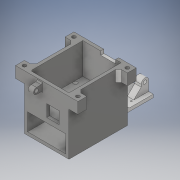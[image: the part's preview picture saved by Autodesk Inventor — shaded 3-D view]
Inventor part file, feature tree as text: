
AUTODESK INVENTOR PART (.ipt)
format: ipt  version: 2018 (Build 220112000, 112)  size: 1,372,160 bytes
history: native  units: in
note: dims shown in document units (in); Inventor stores cm internally (conversion verified against a paired STEP export)
features: sketch x43, extrude x40, move_body x18, direct_edit x15, chamfer x8, fillet x6, thicken_offset x3, delete_face x2, projected_geometry x2
ambient origin geometry x8: Origin, YZ Plane, XZ Plane, XY Plane, X Axis, Y Axis, Z Axis, Center Point
bodies: Solid1 (feature_tree)
feature tree (137):
  extrude  "Extrusion1"  Depth=0.125in
  extrude  "Extrusion2"  Depth=2.2in TaperAngle=0.0deg
  extrude  "Extrusion3"  Depth=0.125in
  extrude  "Extrusion4"  Depth=0.0625in
  sketch  "Sketch6"  dims[d11=0.5in d13=0.55in]
  extrude  "Extrusion6"  Depth=0.55in
  extrude  "Extrusion7"  Depth=0.725in
  extrude  "Extrusion8"  Depth=0.09in
  extrude  "Extrusion9"  Depth=0.125in
  extrude  "Extrusion10"  Depth=0.125in TaperAngle=0.0deg
  extrude  "Extrusion11"  Depth=0.7in
  extrude  "Extrusion12"  Depth=0.5in
  sketch  "Sketch16"  dims[d38=0.05in]
  extrude  "Extrusion13"  Depth=0.05in
  sketch  "Sketch18"  dims[d40=0.45in]
  fillet  "Fillet1"  Radius=0.05in
  chamfer  "Chamfer1"  Distance=0.36in
  chamfer  "Chamfer2"  Distance=0.25in
  extrude  "Extrusion14"  Depth=0.05in
  extrude  "Extrusion15"  Depth=0.35in
  extrude  "Extrusion16"  Depth=0.25in
  fillet  "Fillet2"  Radius=0.25in
  extrude  "Extrusion17"  Depth=0.1in
  chamfer  "Chamfer3"  Distance=0.05in Angle=45.0deg
  extrude  "Extrusion18"  Depth=0.125in
  extrude  "Extrusion19"  Depth=0.05in TaperAngle=0.0deg
  extrude  "Extrusion20"  Depth=0.05in
  extrude  "Extrusion21"  Depth=0.1in
  fillet  "Fillet3"  Radius=0.275in
  fillet  "Fillet4"  Radius=0.36in
  extrude  "Extrusion22"  Depth=0.225in
  extrude  "Extrusion23"  Depth=0.26in TaperAngle=0.0deg
  chamfer  "Chamfer4"  Distance=0.05in
  chamfer  "Chamfer5"  Distance=0.05in Angle=45.0deg
  extrude  "Extrusion24"  Depth=0.05in TaperAngle=0.0deg
  extrude  "Extrusion25"  Depth=0.125in TaperAngle=0.0deg
  extrude  "Extrusion28"  Depth=1.0in
  extrude  "Extrusion29"  Depth=1.0in
  extrude  "Extrusion30"  Depth=0.25in
  extrude  "Extrusion31"  Depth=0.25in
  thicken_offset  "Thicken1"
  thicken_offset  "Thicken2"
  thicken_offset  "Thicken3"
  direct_edit  "Direct Edit1"
  direct_edit  "Direct Edit2"
  direct_edit  "Direct Edit3"
  direct_edit  "Direct Edit4"
  extrude  "Extrusion32"  Depth=0.21in TaperAngle=0.0deg
  fillet  "Fillet5"  Radius=0.5in
  chamfer  "Chamfer7"  Distance=0.63in
  direct_edit  "Direct Edit5"
  direct_edit  "Direct Edit6"
  extrude  "Extrusion33"  Depth=0.25in
  extrude  "Extrusion34"  Depth=0.25in
  extrude  "Extrusion35"  Depth=0.25in
  direct_edit  "Direct Edit7"
  extrude  "Extrusion36"  Depth=0.25in
  direct_edit  "Direct Edit8"
  delete_face  "Delete Face1"
  direct_edit  "Direct Edit9"
  direct_edit  "Direct Edit10"
  extrude  "Extrusion37"  Depth=0.25in
  extrude  "Extrusion38"  Depth=0.25in
  fillet  "Fillet6"  Radius=0.437in
  extrude  "Extrusion39"  Depth=0.1in TaperAngle=0.0deg
  chamfer  "Chamfer9"  Distance=0.344in
  extrude  "Extrusion40"  Depth=0.25in
  extrude  "Extrusion41"  Depth=0.25in
  chamfer  "Chamfer10"  Distance=0.344in
  extrude  "Extrusion42"  Depth=0.1in TaperAngle=0.0deg
  extrude  "Extrusion43"  Depth=0.1in TaperAngle=45.0deg
  direct_edit  "Direct Edit11"
  direct_edit  "Direct Edit12"
  delete_face  "Delete Face2"
  direct_edit  "Direct Edit13"
  direct_edit  "Direct Edit14"
  direct_edit  "Direct Edit15"
  sketch  "Sketch1"  dims[d0=0.125in d1=1.24in]
  sketch  "Sketch2"  dims[d2=0.9in d3=2.2in d4=0.0in]
  sketch  "Sketch3"  dims[d5=0.125in d6=0.0in d7=2.0in]
  sketch  "Sketch4"  dims[d8=0.125in d9=0.0in d10=0.0625in]
  sketch  "Sketch8"  dims[d14=0.125in d15=0.0in d16=0.725in]
  sketch  "Sketch10"  dims[d17=2.06in d21=0.09in]
  sketch  "Sketch11"  dims[d22=0.4in d23=0.0in d24=0.125in]
  sketch  "Sketch12"  dims[d25=1.475in d26=0.0in d27=0.125in d28=0.0in]
  sketch  "Sketch13"  dims[d29=0.6in d30=0.7in]
  sketch  "Sketch14"  dims[d31=0.5in d32=0.0in d33=0.1603in]
  sketch  "Sketch15"  dims[d34=0.5in d35=0.0in d36=0.146in d37=0.05in]
  sketch  "Sketch17"  dims[d39=0.1in]
  sketch  "Sketch19"  dims[d41=1.0in d42=0.36in d43=0.0in]
  sketch  "Sketch20"  dims[d44=0.225in]
  sketch  "Sketch21"  dims[d45=0.146in d46=0.25in d47=0.0in]
  sketch  "Sketch22"  dims[d49=0.05in d50=0.0in d51=0.05in]
  sketch  "Sketch24"  dims[d52=0.05in d53=0.35in]
  sketch  "Sketch25"  dims[d54=0.02in d55=0.02in d56=0.25in]
  sketch  "Sketch26"  dims[d57=0.25in d58=0.1in]
  sketch  "Sketch27"  dims[d59=0.0in]
  sketch  "Sketch28"  dims[d60=0.35in]
  sketch  "Sketch29"  dims[d61=0.346in]
  sketch  "Sketch30"  dims[d62=0.425in]
  sketch  "Sketch31"  dims[d63=0.9in]
  sketch  "Sketch34"  dims[d64=0.123in]
  sketch  "Sketch35"  dims[d65=0.123in d66=0.05in d67=0.125in d68=45.0deg]
  sketch  "Sketch36"  dims[d69=0.05in d70=0.125in d71=45.0deg d72=0.01in]
  sketch  "Sketch37"  dims[d73=0.4in d74=0.05in d75=0.0in]
  projected_geometry  "Projected Loop1"
  sketch  "Sketch38"  dims[d76=0.146in d77=0.05in]
  sketch  "Sketch39"  dims[d78=0.05in d80=0.1in d81=0.275in d82=0.36in d83=0.0in]
  sketch  "Sketch40"  dims[d84=0.225in d85=0.01in]
  sketch  "Sketch41"  dims[d86=0.146in d87=0.26in d88=0.0in]
  sketch  "Sketch42"  dims[d89=0.123in]
  sketch  "Sketch43"  dims[d90=0.05in]
  sketch  "Sketch44"  dims[d91=0.05in d92=0.05in d93=0.0in d94=0.05in d95=0.125in d96=45.0deg]
  sketch  "Sketch45"  dims[d97=0.45in d98=0.05in d99=0.0in]
  sketch  "Sketch46"  dims[d100=0.125in d101=0.0in d102=0.125in d103=0.0in]
  sketch  "Sketch47"  dims[d104=1.0in d105=1.0in]
  projected_geometry  "Projected Loop2"
  sketch  "Sketch48"  dims[d106=1.0in d107=0.912in]
  sketch  "Sketch49"  dims[d108=0.912in d109=0.912in d110=0.912in d111=0.21in d112=0.0in d113=0.5in d114=0.63in d115=0.63in d116=0.63in d117=0.63in d118=0.437in d119=0.437in d120=0.437in d121=0.437in d122=0.1in d123=0.0in d124=0.344in d125=0.344in d126=0.344in d127=0.344in d128=0.1in d129=0.0in d130=0.1in d131=0.125in d132=45.0deg d133=0.05in d134=0.125in d135=45.0deg d139=0.312in d140=0.3603in d141=0.3603in d142=0.3603in d143=0.3603in d144=0.3603in d145=0.45in d146=0.0in d147=0.146in d148=0.146in d149=0.146in d150=0.146in d151=0.5in d152=0.0in d163=1.0in d164=0.0in d165=0.35in d166=1.5in d168=0.3in d169=1.0in d170=0.0in d171=0.05in d172=0.3in d173=0.0in d174=0.05in d175=0.0in d176=0.1in d177=0.1in d178=0.1in d179=0.1in d180=0.1in d181=0.1in d182=0.0in d183=0.0in d184=0.1in d185=0.0in d186=0.0in d187=-0.1in d188=0.0in d189=0.0in d190=-0.05in d191=0.5in d192=0.0in d193=0.0in d194=0.05in d195=0.937in d196=0.937in d197=0.937in d198=0.937in d199=0.375in d200=0.0in d201=0.5in d202=0.125in d203=0.125in d204=45.0deg d205=0.0in d206=0.0in d207=-0.175in d208=0.0in d209=0.0in d210=0.35in d211=0.0in d212=0.0in d213=0.105in d214=0.0in d215=0.0in d216=0.105in d217=0.16in d218=1.0in d219=0.0in d220=3.9056in d221=0.6in d222=0.0in d223=0.0in d224=3.9in d225=0.6in d226=1.0in d227=0.0in d228=0.0in d229=0.0in d230=0.2in d231=0.0in d232=0.0in d233=0.0in d234=0.0in d235=0.7in d236=0.0in d237=0.0in d238=-0.065in d239=0.0in d240=0.0in d241=-1.54in d242=0.125in d243=0.9in d244=1.5in d245=0.0in d249=0.26in d250=0.3in d251=0.19in d252=0.55in d253=0.0in d254=0.15in d255=0.146in d256=0.36in d257=0.0in d258=0.3in d259=0.125in d260=45.0deg d261=0.1in d262=0.0in d263=0.1in d264=0.0in d265=0.1in d266=0.125in d267=45.0deg d268=0.6in d269=0.15in d270=0.0in d271=0.1in d272=0.0in d273=0.06in d274=0.06in d275=0.25in d276=0.25in d277=0.1in d278=0.0in d279=45.0deg d280=0.75in d281=0.2in d282=0.0in d283=0.0in d284=0.0in d285=0.0in d286=0.02in d287=0.0in d288=0.0in d289=0.09in d290=0.25in d291=0.0in d292=0.0in d293=0.0in d294=0.3in d295=0.0in d296=0.25in d297=0.0in d298=0.0in]
  move_body  "Move1"
  move_body  "Move2"
  move_body  "Move3"
  move_body  "Move4"
  move_body  "Move5"
  move_body  "Move6"
  move_body  "Move7"
  move_body  "Move8"
  move_body  "Move9"
  move_body  "Move10"
  move_body  "Move11"
  move_body  "Move12"
  move_body  "Move13"
  move_body  "Move14"
  move_body  "Move15"
  move_body  "Move16"
  move_body  "Move17"
  move_body  "Move18"
